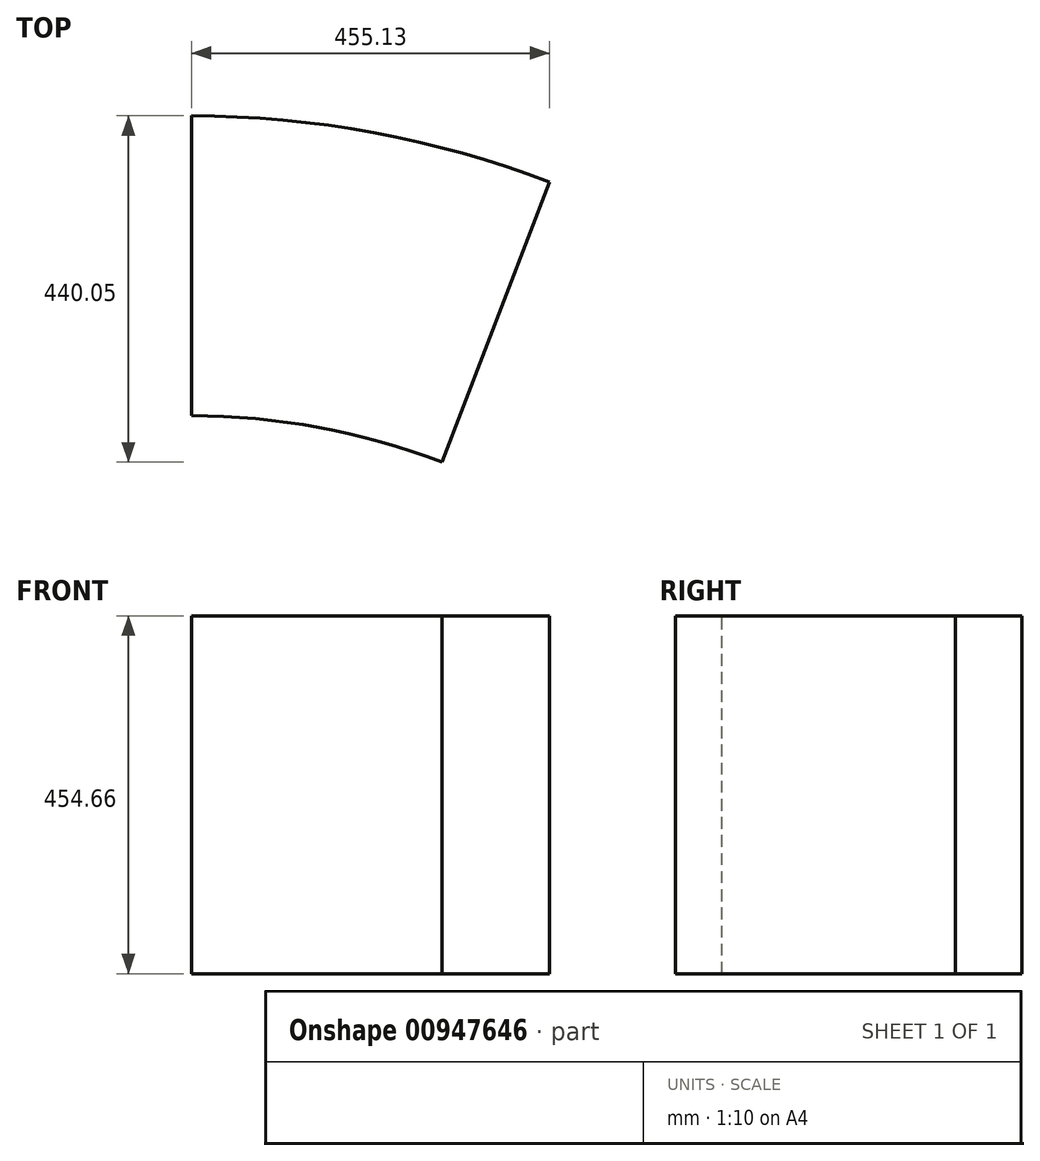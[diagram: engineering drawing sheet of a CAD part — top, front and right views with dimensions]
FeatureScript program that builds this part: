
annotation { "Feature Type Name" : "Feature", "Feature Type Description" : "" }
export const myFeature = defineFeature(function(context is Context, id is Id, definition is map)
    precondition{}
    {
        {
            var Q0;
            Q0=qCreatedBy(makeId("Top.planeOp"),FACE);
            var sketch = newSketch(context, id + "F0", { "sketchPlane" : qUnion([Q0])});
            skCircle(sketch, "E0", {"center": v(0, 0) * mm, "radius": 1270 * mm});
            skCircle(sketch, "E1", {"center": v(0, 0) * mm, "radius": 889 * mm});
            skSolve(sketch);
        }
        {
            var Q0;
            Q0=qCreatedBy(makeId("Top.planeOp"),FACE);
            var Q1;
            Q1=qCreatedBy(makeId("Top.planeOp"),FACE);
            var sketch = newSketch(context, id + "F1", { "sketchPlane" : qUnion([Q0, Q1])});
            skLineSegment(sketch, "E2", {"start": v(0, 889) * mm, "end": v(0, 1270) * mm});
            skLineSegment(sketch, "E3", {"start": v(318.59, 829.95) * mm, "end": v(455.13, 1185.65) * mm});
            skArc(sketch, "E4.0", {"start": v(455.13, 1185.65) * mm, "mid": v(231.44, 1248.73) * mm, "end": v(0, 1270) * mm});
            skArc(sketch, "E5.0", {"start": v(318.59, 829.95) * mm, "mid": v(162, 874.11) * mm, "end": v(0, 889) * mm});
            skSolve(sketch);
        }
        {
            var Q0;
            Q0 = qSketchRegion(id + "F1", true);
            extrude(context, id + "F2", {"entities" : qUnion([Q0]), "oppositeDirection" : true, "depth" : 454.66 * mm, "offsetDistance" : 25.4 * mm});
        }
    });
